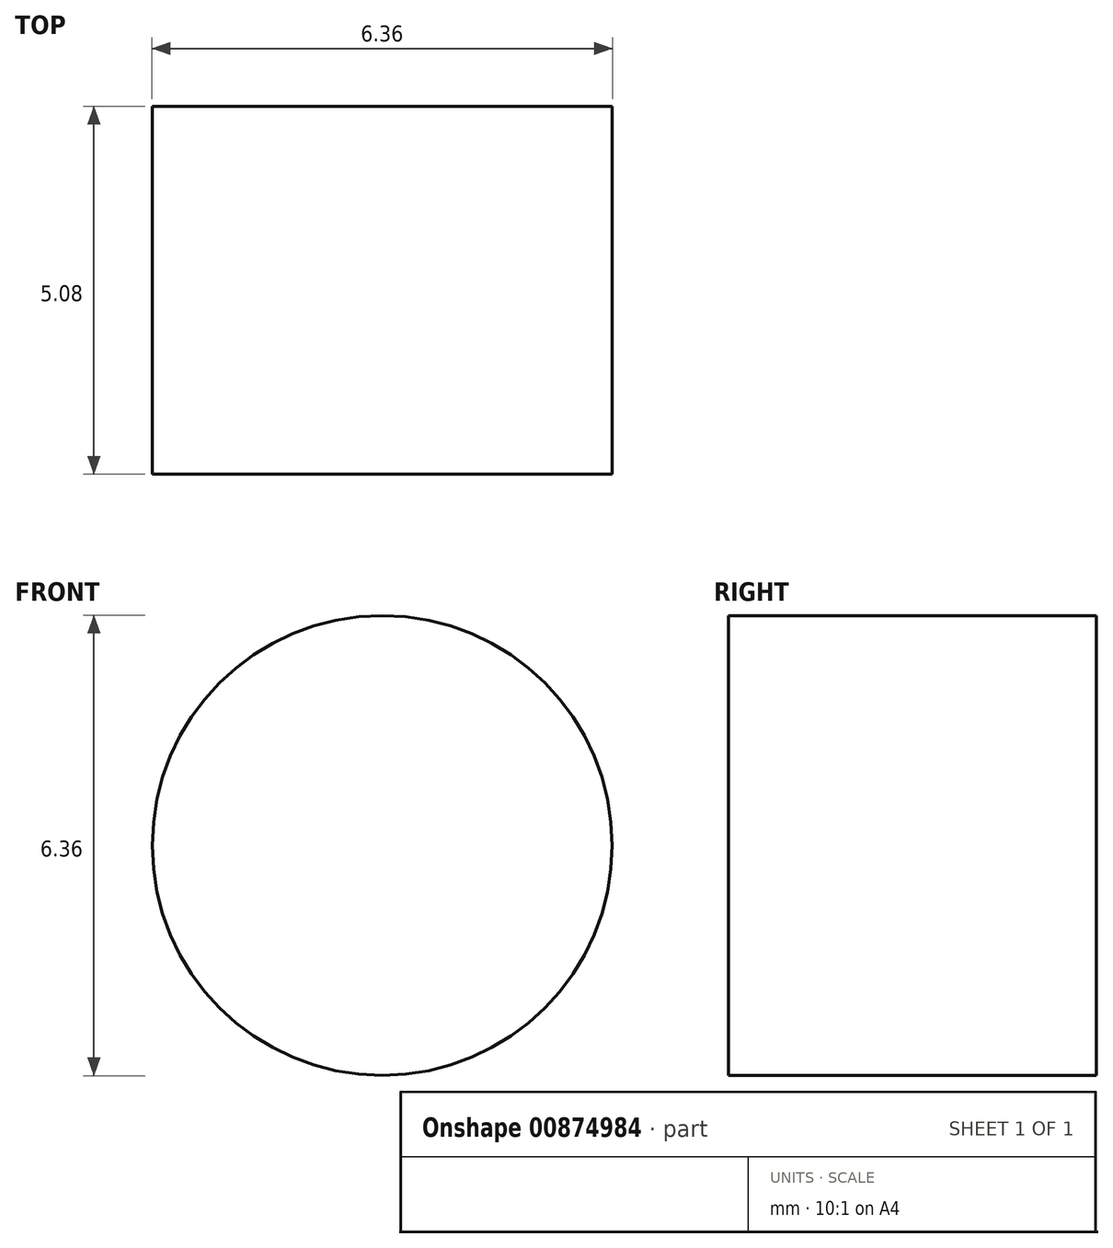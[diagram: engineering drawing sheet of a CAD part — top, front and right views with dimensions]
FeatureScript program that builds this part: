
annotation { "Feature Type Name" : "Feature", "Feature Type Description" : "" }
export const myFeature = defineFeature(function(context is Context, id is Id, definition is map)
    precondition{}
    {
        {
            var Q0;
            Q0=qCreatedBy(makeId("Front.planeOp"),FACE);
            var sketch = newSketch(context, id + "F0", { "sketchPlane" : qUnion([Q0])});
            skCircle(sketch, "E0", {"center": v(0, 0) * mm, "radius": 3.18 * mm});
            skSolve(sketch);
        }
        {
            var Q0;
            Q0=makeQuery(id+"F0.imprint","IMPRINT",FACE,{"disambiguationData":[TD([[makeQuery(id+"F0.imprint","IMPRINT",EDGE,{"derivedFrom":sQuery(id+"F0.wireOp",EDGE,"E0")}),1.0]])]});
            extrude(context, id + "F1", {"entities" : qUnion([Q0]), "depth" : 5.08 * mm, "offsetDistance" : 25.4 * mm});
        }
    });
